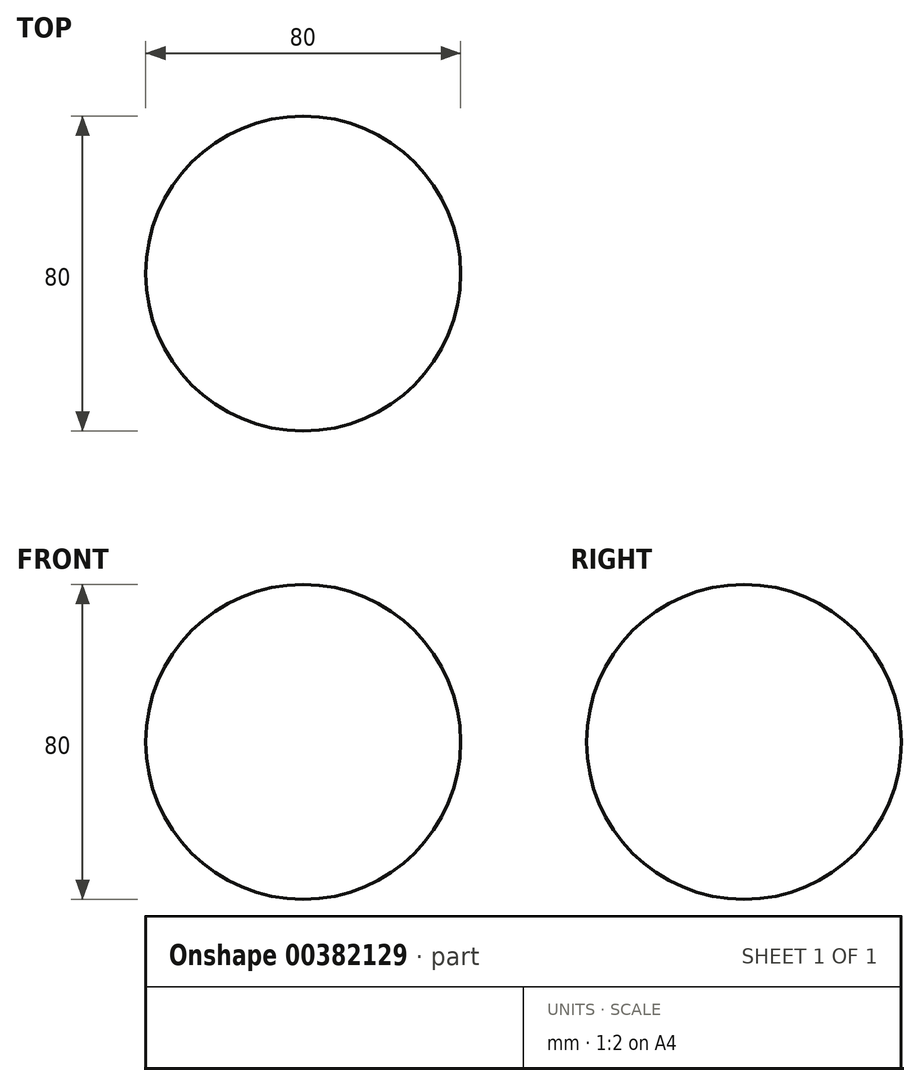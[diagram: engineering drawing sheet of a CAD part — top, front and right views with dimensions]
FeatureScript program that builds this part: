
annotation { "Feature Type Name" : "Feature", "Feature Type Description" : "" }
export const myFeature = defineFeature(function(context is Context, id is Id, definition is map)
    precondition{}
    {
        {
            var Q0;
            Q0=qCreatedBy(makeId("Front.planeOp"),FACE);
            var sketch = newSketch(context, id + "F0", { "sketchPlane" : qUnion([Q0])});
            skLineSegment(sketch, "E0", {"start": v(-40, 0) * mm, "end": v(40, 0) * mm, "construction": true});
            skArc(sketch, "E1", {"start": v(40, 0) * mm, "mid": v(0, 40) * mm, "end": v(-40, 0) * mm});
            skLineSegment(sketch, "E2", {"start": v(-40, 0) * mm, "end": v(40, 0) * mm});
            skSolve(sketch);
        }
        {
            var Q0;
            Q0=makeQuery(id+"F0.imprint","IMPRINT",FACE,{"disambiguationData":[TD([[makeQuery(id+"F0.imprint","IMPRINT",EDGE,{"derivedFrom":sQuery(id+"F0.wireOp",EDGE,"E1")}),1.0]])]});
            var Q1;
            Q1=sQuery(id+"F0.wireOp",EDGE,"E2");
            revolve(context, id + "F1", {"entities" : qUnion([Q0]), "axis" : qUnion([Q1]), "revolveType" : RevolveType.FULL});
        }
    });
